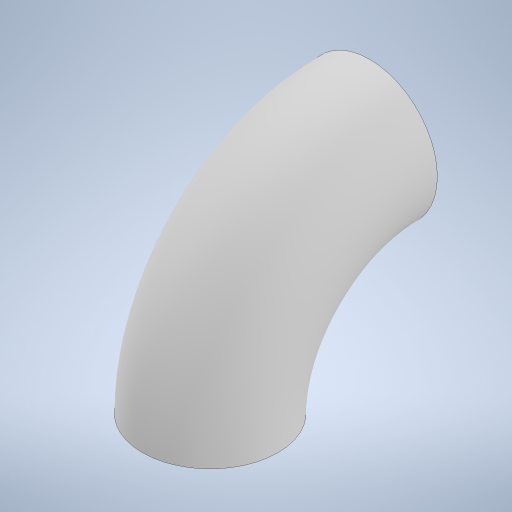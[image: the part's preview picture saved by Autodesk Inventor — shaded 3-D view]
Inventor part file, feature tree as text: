
AUTODESK INVENTOR PART (.ipt)
format: ipt  version: 2023 (Build 270158000, 158)  size: 263,680 bytes
history: native  units: mm
features: sketch x2, sweep x1
ambient origin geometry x8: Origin, YZ Plane, XZ Plane, XY Plane, X Axis, Y Axis, Z Axis, Center Point
bodies: Solido1 (feature_tree)
feature tree (3):
  sweep  "Sweep1"
  sketch  "Schizzo1"
  sketch  "Schizzo2"
